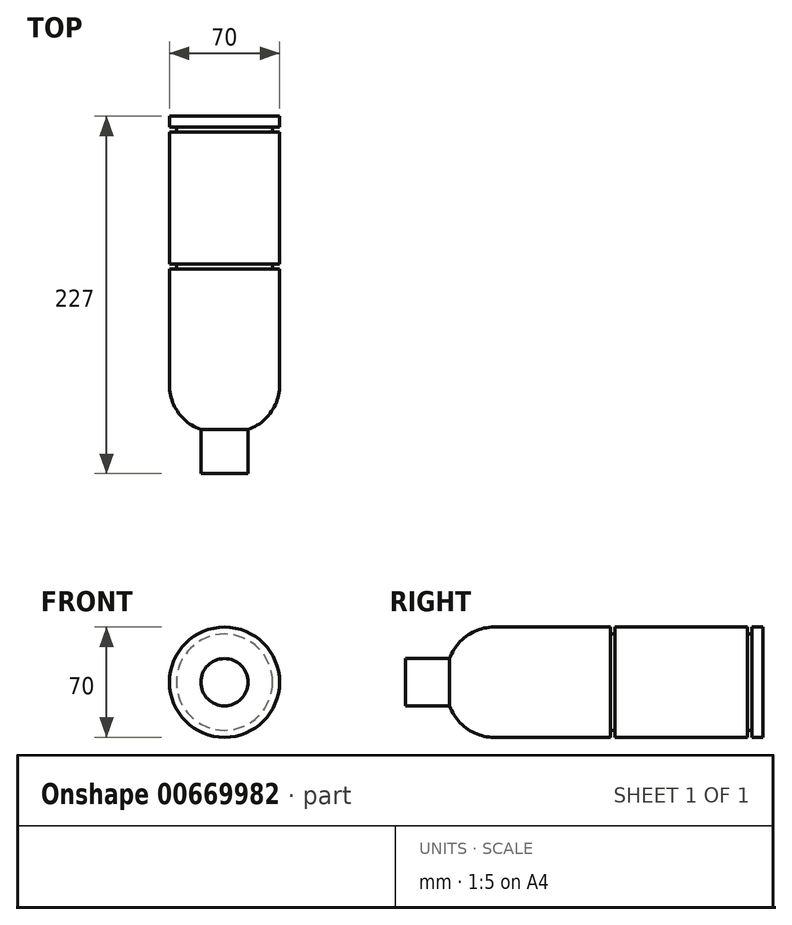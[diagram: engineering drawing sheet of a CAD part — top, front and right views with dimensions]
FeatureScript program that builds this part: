
annotation { "Feature Type Name" : "Feature", "Feature Type Description" : "" }
export const myFeature = defineFeature(function(context is Context, id is Id, definition is map)
    precondition{}
    {
        {
            var Q0;
            Q0=qCreatedBy(makeId("Front.planeOp"),FACE);
            var sketch = newSketch(context, id + "F0", { "sketchPlane" : qUnion([Q0])});
            skCircle(sketch, "E0", {"center": v(0, 0) * mm, "radius": 35 * mm});
            skSolve(sketch);
        }
        {
            var Q0;
            Q0 = qSketchRegion(id + "F0", true);
            extrude(context, id + "F1", {"entities" : qUnion([Q0]), "depth" : 230 * mm, "offsetDistance" : 25.4 * mm});
        }
        {
            var Q0;
            Q0=makeQuery(id+"F1.opExtrude","CAP_FACE",FACE,{"disambiguationData":[OSD([sQuery(id+"F0.wireOp",EDGE,"E0")])],"isStart":true});
            cPlane(context, id + "F2", {"entities" : qUnion([Q0]), "cplaneType" : CPlaneType.OFFSET, "offset" : 10 * mm, "oppositeDirection" : true, "width" : 152.4 * mm, "height" : 152.4 * mm});
        }
        {
            var Q0;
            Q0=qCreatedBy(id+"F2.planeOp",FACE);
            var sketch = newSketch(context, id + "F3", { "sketchPlane" : qUnion([Q0])});
            skCircle(sketch, "E1", {"center": v(0, 0) * mm, "radius": 30.5 * mm});
            skCircle(sketch, "E2", {"center": v(0, 0) * mm, "radius": 40.5 * mm});
            skSolve(sketch);
        }
        {
            var Q0;
            Q0 = qSketchRegion(id + "F3", true);
            var Q1;
            Q1 = qSketchRegion(id + "F0", true);
            extrude(context, id + "F4", {"entities" : qUnion([Q0, Q1]), "operationType" : NewBodyOperationType.REMOVE, "oppositeDirection" : true, "depth" : 3 * mm, "offsetDistance" : 25.4 * mm});
        }
        {
            var Q0;
            Q0=makeQuery(id+"F4.boolean.opBoolean","COPY",FACE,{"derivedFrom":makeQuery(id+"F4.opExtrude","CAP_FACE",FACE,{"disambiguationData":[OSD([sQuery(id+"F0.wireOp",EDGE,"E0")])],"isStart":false})});
            cPlane(context, id + "F5", {"entities" : qUnion([Q0]), "cplaneType" : CPlaneType.OFFSET, "offset" : 94 * mm, "oppositeDirection" : true, "width" : 152.4 * mm, "height" : 152.4 * mm});
        }
        {
            var Q0;
            Q0=qCreatedBy(id+"F5.planeOp",FACE);
            var sketch = newSketch(context, id + "F6", { "sketchPlane" : qUnion([Q0])});
            skCircle(sketch, "E3", {"center": v(0, 0) * mm, "radius": 30.5 * mm});
            skCircle(sketch, "E4", {"center": v(0, 0) * mm, "radius": 36.68 * mm});
            skSolve(sketch);
        }
        {
            var Q0;
            Q0 = qSketchRegion(id + "F6", true);
            extrude(context, id + "F7", {"entities" : qUnion([Q0]), "operationType" : NewBodyOperationType.REMOVE, "oppositeDirection" : true, "depth" : 3 * mm, "offsetDistance" : 25.4 * mm});
        }
        {
            var Q0;
            Q0=makeQuery(id+"F1.opExtrude","CAP_FACE",FACE,{"disambiguationData":[OSD([sQuery(id+"F0.wireOp",EDGE,"E0")])],"isStart":false});
            var sketch = newSketch(context, id + "F8", { "sketchPlane" : qUnion([Q0])});
            skCircle(sketch, "E5", {"center": v(0, 0) * mm, "radius": 15 * mm});
            skCircle(sketch, "E6", {"center": v(0, 0) * mm, "radius": 38.38 * mm});
            skSolve(sketch);
        }
        {
            var Q0;
            Q0 = qSketchRegion(id + "F8", true);
            extrude(context, id + "F9", {"entities" : qUnion([Q0]), "operationType" : NewBodyOperationType.REMOVE, "oppositeDirection" : true, "depth" : 28 * mm, "offsetDistance" : 25.4 * mm});
        }
        {
            var Q0;
            {var subQ0=sQuery(id+"F0.wireOp",EDGE,"E0");var subQ1=makeQuery(id+"F1.opExtrude","CAP_FACE",FACE,{"disambiguationData":[OSD([subQ0])],"isStart":false});Q0=makeQuery(id+"F9.boolean.opBoolean","INTERSECT",EDGE,{"derivedFrom":[makeQuery(id+"F7.boolean.opBoolean","SPLIT",FACE,{"disambiguationData":[TD([subQ1])],"derivedFrom":makeQuery(id+"F4.boolean.opBoolean","SPLIT",FACE,{"disambiguationData":[TD([subQ1])],"derivedFrom":makeQuery(id+"F1.opExtrude","SWEPT_FACE",FACE,{"disambiguationData":[OSD([subQ0])]})})}),makeQuery(id+"F9.opExtrude","CAP_FACE",FACE,{"disambiguationData":[OSD([sQuery(id+"F8.wireOp",EDGE,"E5"),sQuery(id+"F8.wireOp",EDGE,"E6")])],"isStart":false})]});}
            fillet(context, id + "F10", {"entities" : qUnion([Q0]), "radius" : 30 * mm, "tangentPropagation" : true, "allowEdgeOverflow" : false});
        }
    });
